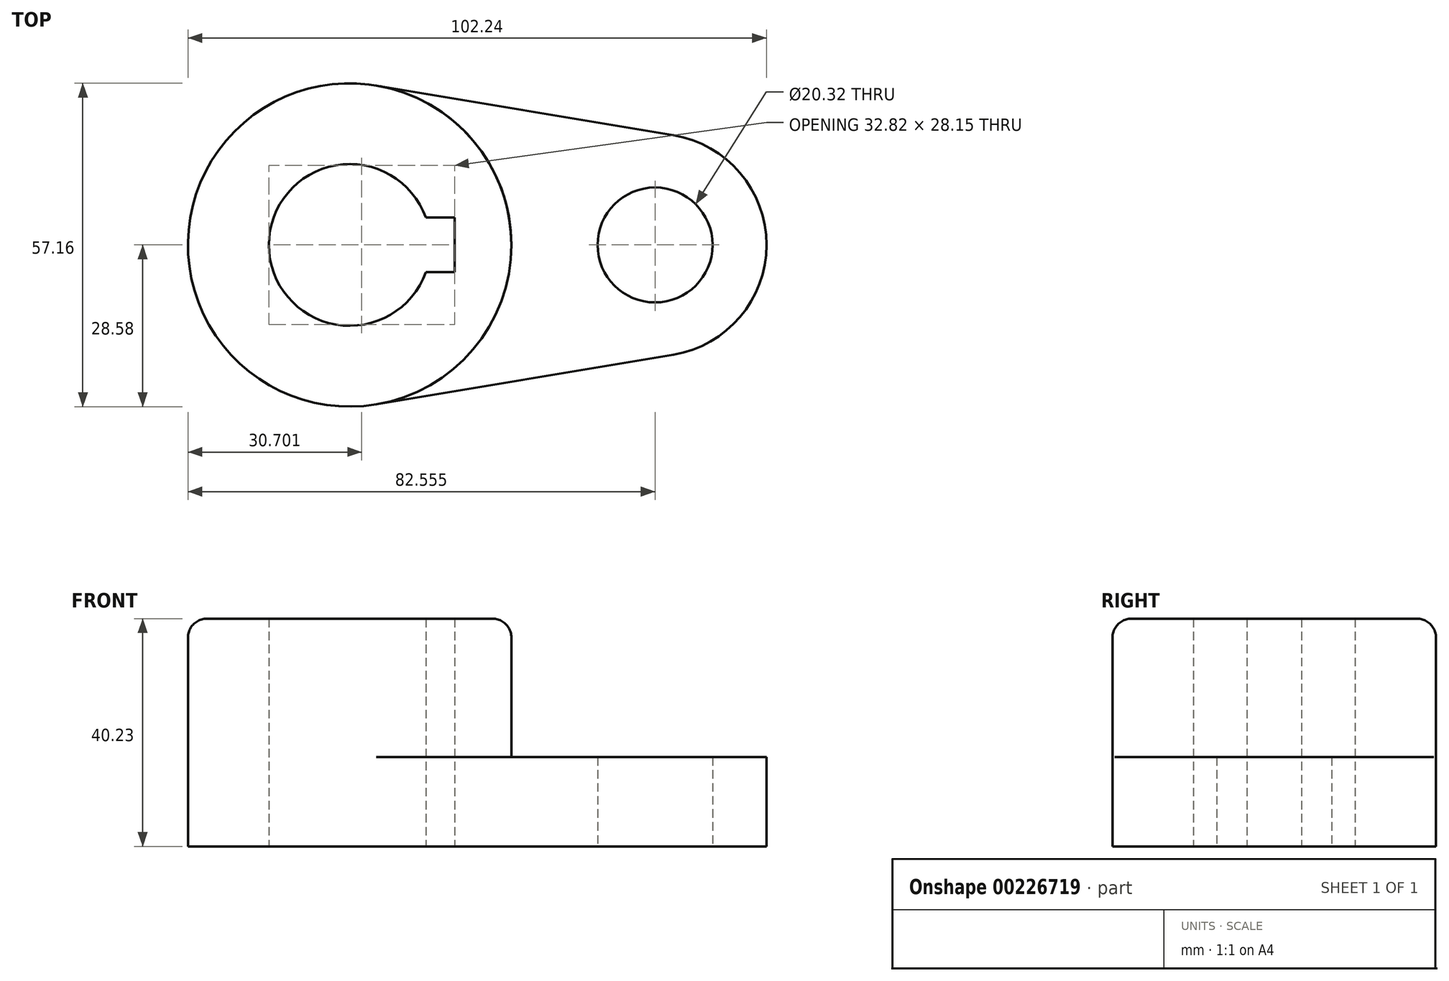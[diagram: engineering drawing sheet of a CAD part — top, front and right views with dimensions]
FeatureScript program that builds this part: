
annotation { "Feature Type Name" : "Feature", "Feature Type Description" : "" }
export const myFeature = defineFeature(function(context is Context, id is Id, definition is map)
    precondition{}
    {
        {
            var Q0;
            Q0=qCreatedBy(makeId("Top.planeOp"),FACE);
            var sketch = newSketch(context, id + "F0", { "sketchPlane" : qUnion([Q0])});
            skCircle(sketch, "E0", {"center": v(0, 0) * mm, "radius": 14.29 * mm});
            skCircle(sketch, "E1", {"center": v(0, 0) * mm, "radius": 28.58 * mm});
            skLineSegment(sketch, "E2.bottom", {"start": v(18.53, 4.83) * mm, "end": v(-18.53, 4.83) * mm});
            skLineSegment(sketch, "E2.top", {"start": v(18.53, -4.83) * mm, "end": v(-18.53, -4.83) * mm});
            skLineSegment(sketch, "E2.left", {"start": v(18.53, 4.83) * mm, "end": v(18.53, -4.83) * mm});
            skLineSegment(sketch, "E2.right", {"start": v(-18.53, 4.83) * mm, "end": v(-18.53, -4.83) * mm});
            skSolve(sketch);
        }
        {
            var Q0;
            {var subQ5=sQuery(id+"F0.wireOp",EDGE,"E2.right");Q0=makeQuery(id+"F0.imprint","IMPRINT",FACE,{"disambiguationData":[TD([[makeQuery(id+"F0.imprint","IMPRINT",EDGE,{"derivedFrom":subQ5}),1.0]])]});}
            var Q1;
            Q1=makeQuery(id+"F0.imprint","IMPRINT",FACE,{"disambiguationData":[TD([[makeQuery(id+"F0.imprint","IMPRINT",EDGE,{"derivedFrom":sQuery(id+"F0.wireOp",EDGE,"E1")}),1.0]])]});
            extrude(context, id + "F1", {"entities" : qUnion([Q0, Q1]), "depth" : 40.23 * mm});
        }
        {
            var Q0;
            Q0=qCreatedBy(makeId("Top.planeOp"),FACE);
            var sketch = newSketch(context, id + "F2", { "sketchPlane" : qUnion([Q0])});
            skLineSegment(sketch, "E3", {"start": v(0, 0) * mm, "end": v(53.98, 0) * mm, "construction": true});
            skCircle(sketch, "E4", {"center": v(53.98, 0) * mm, "radius": 10.16 * mm});
            skCircle(sketch, "E5", {"center": v(53.98, 0) * mm, "radius": 19.69 * mm});
            skLineSegment(sketch, "E6", {"start": v(4.7, 28.18) * mm, "end": v(57.22, 19.42) * mm});
            skLineSegment(sketch, "E7", {"start": v(57.22, -19.42) * mm, "end": v(4.7, -28.18) * mm});
            skCircle(sketch, "E8.0", {"center": v(0, 0) * mm, "radius": 28.58 * mm});
            skPoint(sketch, "E9.orphan", {"position": v(0, 28.97) * mm});
            skPoint(sketch, "E10.orphan", {"position": v(0, -28.97) * mm});
            skSolve(sketch);
        }
        {
            var Q0;
            {var subQ0=sQuery(id+"F2.wireOp",EDGE,"3cXsBSU8-Gt2v-teSw-7KUJ-TvDPJw7lKMj7");var subQ1=sQuery(id+"F2.wireOp",EDGE,"E6");var subQ2=makeQuery(id+"F2.imprint","INTERSECT",VERTEX,{"disambiguationData":[OD(0.0)],"derivedFrom":[subQ1,subQ0]});Q0=makeQuery(id+"F2.imprint","IMPRINT",FACE,{"disambiguationData":[TD([[makeQuery(id+"F2.imprint","IMPRINT",EDGE,{"disambiguationData":[TD([[subQ2,-1.0]])],"derivedFrom":subQ1}),1.0]])]});}
            var Q1;
            {var subQ0=sQuery(id+"F2.wireOp",EDGE,"3cXsBSU8-Gt2v-teSw-7KUJ-TvDPJw7lKMj7");var subQ1=sQuery(id+"F2.wireOp",EDGE,"E7");var subQ2=makeQuery(id+"F2.imprint","INTERSECT",VERTEX,{"disambiguationData":[OD(0.0)],"derivedFrom":[subQ1,subQ0]});Q1=makeQuery(id+"F2.imprint","IMPRINT",FACE,{"disambiguationData":[TD([[makeQuery(id+"F2.imprint","IMPRINT",EDGE,{"disambiguationData":[TD([[subQ2,1.0]])],"derivedFrom":subQ1}),1.0]])]});}
            var Q2;
            Q2=makeQuery(id+"F2.imprint","IMPRINT",FACE,{"disambiguationData":[TD([[makeQuery(id+"F2.imprint","IMPRINT",EDGE,{"derivedFrom":sQuery(id+"F2.wireOp",EDGE,"E4")}),-1.0]])]});
            var Q3;
            {var subQ0=sQuery(id+"F2.wireOp",EDGE,"E6");var subQ1=sQuery(id+"F2.wireOp",EDGE,"E5");var subQ2=makeQuery(id+"F2.imprint","INTERSECT",VERTEX,{"derivedFrom":[subQ1,subQ0]});Q3=makeQuery(id+"F2.imprint","IMPRINT",FACE,{"disambiguationData":[TD([[makeQuery(id+"F2.imprint","IMPRINT",EDGE,{"disambiguationData":[TD([[subQ2,-1.0]])],"derivedFrom":subQ1}),-1.0]])]});}
            extrude(context, id + "F3", {"entities" : qUnion([Q0, Q1, Q2, Q3]), "operationType" : NewBodyOperationType.ADD, "depth" : 15.77 * mm});
        }
        {
            var Q0;
            Q0=makeQuery(id+"F1.opExtrude","CAP_EDGE",EDGE,{"disambiguationData":[OSD([sQuery(id+"F0.wireOp",EDGE,"E1")])],"isStart":false});
            fillet(context, id + "F4", {"entities" : qUnion([Q0]), "radius" : 3.3 * mm, "tangentPropagation" : true, "allowEdgeOverflow" : false});
        }
    });
